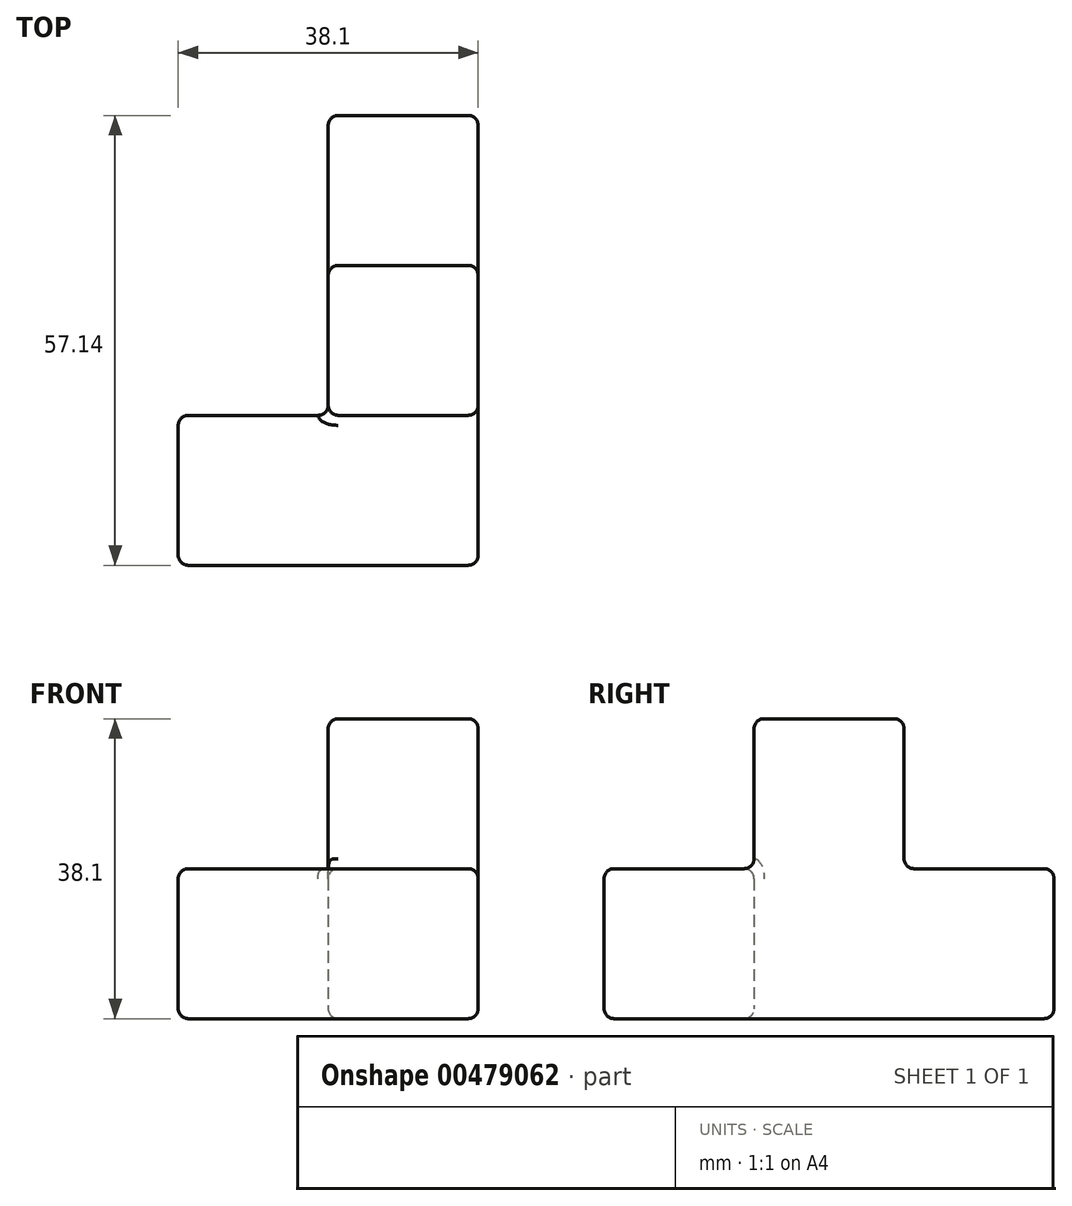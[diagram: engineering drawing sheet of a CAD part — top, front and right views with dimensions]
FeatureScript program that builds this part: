
annotation { "Feature Type Name" : "Feature", "Feature Type Description" : "" }
export const myFeature = defineFeature(function(context is Context, id is Id, definition is map)
    precondition{}
    {
        {
            var Q0;
            Q0=qCreatedBy(makeId("Top.planeOp"),FACE);
            var sketch = newSketch(context, id + "F0", { "sketchPlane" : qUnion([Q0])});
            skLineSegment(sketch, "E0.bottom", {"start": v(-19.05, -28.57) * mm, "end": v(19.05, -28.57) * mm});
            skLineSegment(sketch, "E0.top", {"start": v(0, 28.58) * mm, "end": v(19.05, 28.58) * mm});
            skLineSegment(sketch, "E0.left", {"start": v(-19.05, -28.57) * mm, "end": v(-19.05, -9.52) * mm});
            skLineSegment(sketch, "E0.right", {"start": v(19.05, -28.58) * mm, "end": v(19.05, 28.58) * mm});
            skPoint(sketch, "E0.middle", {"position": v(0, 0) * mm});
            skLineSegment(sketch, "E1.top", {"start": v(0, -9.52) * mm, "end": v(-19.05, -9.52) * mm});
            skLineSegment(sketch, "E1.left", {"start": v(0, 28.58) * mm, "end": v(0, -9.52) * mm});
            skPoint(sketch, "E2.orphan", {"position": v(-19.05, 28.58) * mm});
            skSolve(sketch);
        }
        {
            var Q0;
            Q0 = qSketchRegion(id + "F0", true);
            extrude(context, id + "F1", {"entities" : qUnion([Q0]), "endBound" : BoundingType.SYMMETRIC, "depth" : 19.05 * mm});
        }
        {
            var Q0;
            Q0=makeQuery(id+"F1.opExtrude","CAP_FACE",FACE,{"disambiguationData":[OSD([sQuery(id+"F0.wireOp",EDGE,"E0.bottom"),sQuery(id+"F0.wireOp",EDGE,"E0.top"),sQuery(id+"F0.wireOp",EDGE,"E0.left"),sQuery(id+"F0.wireOp",EDGE,"E0.right"),sQuery(id+"F0.wireOp",EDGE,"E1.top"),sQuery(id+"F0.wireOp",EDGE,"E1.left")])],"isStart":false});
            var sketch = newSketch(context, id + "F2", { "sketchPlane" : qUnion([Q0])});
            skLineSegment(sketch, "E3.bottom", {"start": v(0, -9.52) * mm, "end": v(19.05, -9.52) * mm});
            skLineSegment(sketch, "E3.top", {"start": v(0, 9.53) * mm, "end": v(19.05, 9.53) * mm});
            skLineSegment(sketch, "E3.left", {"start": v(0, -9.52) * mm, "end": v(0, 9.53) * mm});
            skLineSegment(sketch, "E3.right", {"start": v(19.05, -9.52) * mm, "end": v(19.05, 9.53) * mm});
            skSolve(sketch);
        }
        {
            var Q0;
            Q0 = qSketchRegion(id + "F2", true);
            extrude(context, id + "F3", {"entities" : qUnion([Q0]), "operationType" : NewBodyOperationType.ADD, "depth" : 19.05 * mm});
        }
        {
            var Q0;
            Q0=makeQuery(id+"F3.boolean.opBoolean","MERGE",FACE,{"derivedFrom":[makeQuery(id+"F1.opExtrude","SWEPT_FACE",FACE,{"disambiguationData":[OSD([sQuery(id+"F0.wireOp",EDGE,"E0.right")])]}),makeQuery(id+"F3.opExtrude","SWEPT_FACE",FACE,{"disambiguationData":[OSD([sQuery(id+"F2.wireOp",EDGE,"E3.right")])]})]});
            var Q1;
            Q1=makeQuery(id+"F1.opExtrude","SWEPT_FACE",FACE,{"disambiguationData":[OSD([sQuery(id+"F0.wireOp",EDGE,"E0.bottom")])]});
            var Q2;
            Q2=makeQuery(id+"F1.opExtrude","SWEPT_FACE",FACE,{"disambiguationData":[OSD([sQuery(id+"F0.wireOp",EDGE,"E0.left")])]});
            var Q3;
            Q3=makeQuery(id+"F1.opExtrude","SWEPT_EDGE",EDGE,{"disambiguationData":[OSD([sQuery(id+"F0.wireOp",EDGE,"E0.left"),sQuery(id+"F0.wireOp",EDGE,"E1.top")])]});
            var Q4;
            Q4=makeQuery(id+"F1.opExtrude","CAP_EDGE",EDGE,{"disambiguationData":[OSD([sQuery(id+"F0.wireOp",EDGE,"E1.top")])],"isStart":true});
            var Q5;
            Q5=makeQuery(id+"F3.opExtrude","CAP_FACE",FACE,{"disambiguationData":[OSD([sQuery(id+"F2.wireOp",EDGE,"E3.bottom"),sQuery(id+"F2.wireOp",EDGE,"E3.top"),sQuery(id+"F2.wireOp",EDGE,"E3.left"),sQuery(id+"F2.wireOp",EDGE,"E3.right")])],"isStart":false});
            var Q6;
            Q6=makeQuery(id+"F3.opExtrude","SWEPT_FACE",FACE,{"disambiguationData":[OSD([sQuery(id+"F2.wireOp",EDGE,"E3.top")])]});
            var Q7;
            {var subQ0=sQuery(id+"F0.wireOp",EDGE,"E1.left");var subQ1=sQuery(id+"F0.wireOp",EDGE,"E0.right");var subQ2=sQuery(id+"F0.wireOp",EDGE,"E0.top");Q7=makeQuery(id+"F3.boolean.opBoolean","SPLIT",FACE,{"disambiguationData":[TD([makeQuery(id+"F1.opExtrude","SWEPT_FACE",FACE,{"disambiguationData":[OSD([subQ2])]})])],"derivedFrom":makeQuery(id+"F1.opExtrude","CAP_FACE",FACE,{"disambiguationData":[OSD([sQuery(id+"F0.wireOp",EDGE,"E0.bottom"),subQ2,sQuery(id+"F0.wireOp",EDGE,"E0.left"),subQ1,sQuery(id+"F0.wireOp",EDGE,"E1.top"),subQ0])],"isStart":false})});}
            var Q8;
            Q8=makeQuery(id+"F1.opExtrude","SWEPT_FACE",FACE,{"disambiguationData":[OSD([sQuery(id+"F0.wireOp",EDGE,"E0.top")])]});
            var Q9;
            Q9=makeQuery(id+"F1.opExtrude","CAP_EDGE",EDGE,{"disambiguationData":[OSD([sQuery(id+"F0.wireOp",EDGE,"E1.left")])],"isStart":true});
            var Q10;
            Q10=makeQuery(id+"F1.opExtrude","CAP_EDGE",EDGE,{"disambiguationData":[OSD([sQuery(id+"F0.wireOp",EDGE,"E1.top")])],"isStart":false});
            var Q11;
            {var subQ0=sQuery(id+"F0.wireOp",EDGE,"E1.top");var subQ1=sQuery(id+"F0.wireOp",EDGE,"E0.left");var subQ2=sQuery(id+"F0.wireOp",EDGE,"E0.right");var subQ3=sQuery(id+"F0.wireOp",EDGE,"E0.bottom");var subQ4=sQuery(id+"F0.wireOp",EDGE,"E1.left");Q11=makeQuery(id+"F3.boolean.opBoolean","SPLIT",FACE,{"disambiguationData":[TD([makeQuery(id+"F1.opExtrude","SWEPT_FACE",FACE,{"disambiguationData":[OSD([subQ3])]})])],"derivedFrom":makeQuery(id+"F1.opExtrude","CAP_FACE",FACE,{"disambiguationData":[OSD([subQ3,sQuery(id+"F0.wireOp",EDGE,"E0.top"),subQ1,subQ2,subQ0,subQ4])],"isStart":false})});}
            var Q12;
            Q12=makeQuery(id+"F3.boolean.opBoolean","MERGE",FACE,{"derivedFrom":[makeQuery(id+"F1.opExtrude","SWEPT_FACE",FACE,{"disambiguationData":[OSD([sQuery(id+"F0.wireOp",EDGE,"E1.left")])]}),makeQuery(id+"F3.opExtrude","SWEPT_FACE",FACE,{"disambiguationData":[OSD([sQuery(id+"F2.wireOp",EDGE,"E3.left")])]})]});
            fillet(context, id + "F4", {"entities" : qUnion([Q0, Q1, Q2, Q3, Q4, Q5, Q6, Q7, Q8, Q9, Q10, Q11, Q12]), "radius" : 1.27 * mm, "tangentPropagation" : true, "allowEdgeOverflow" : false});
        }
    });
